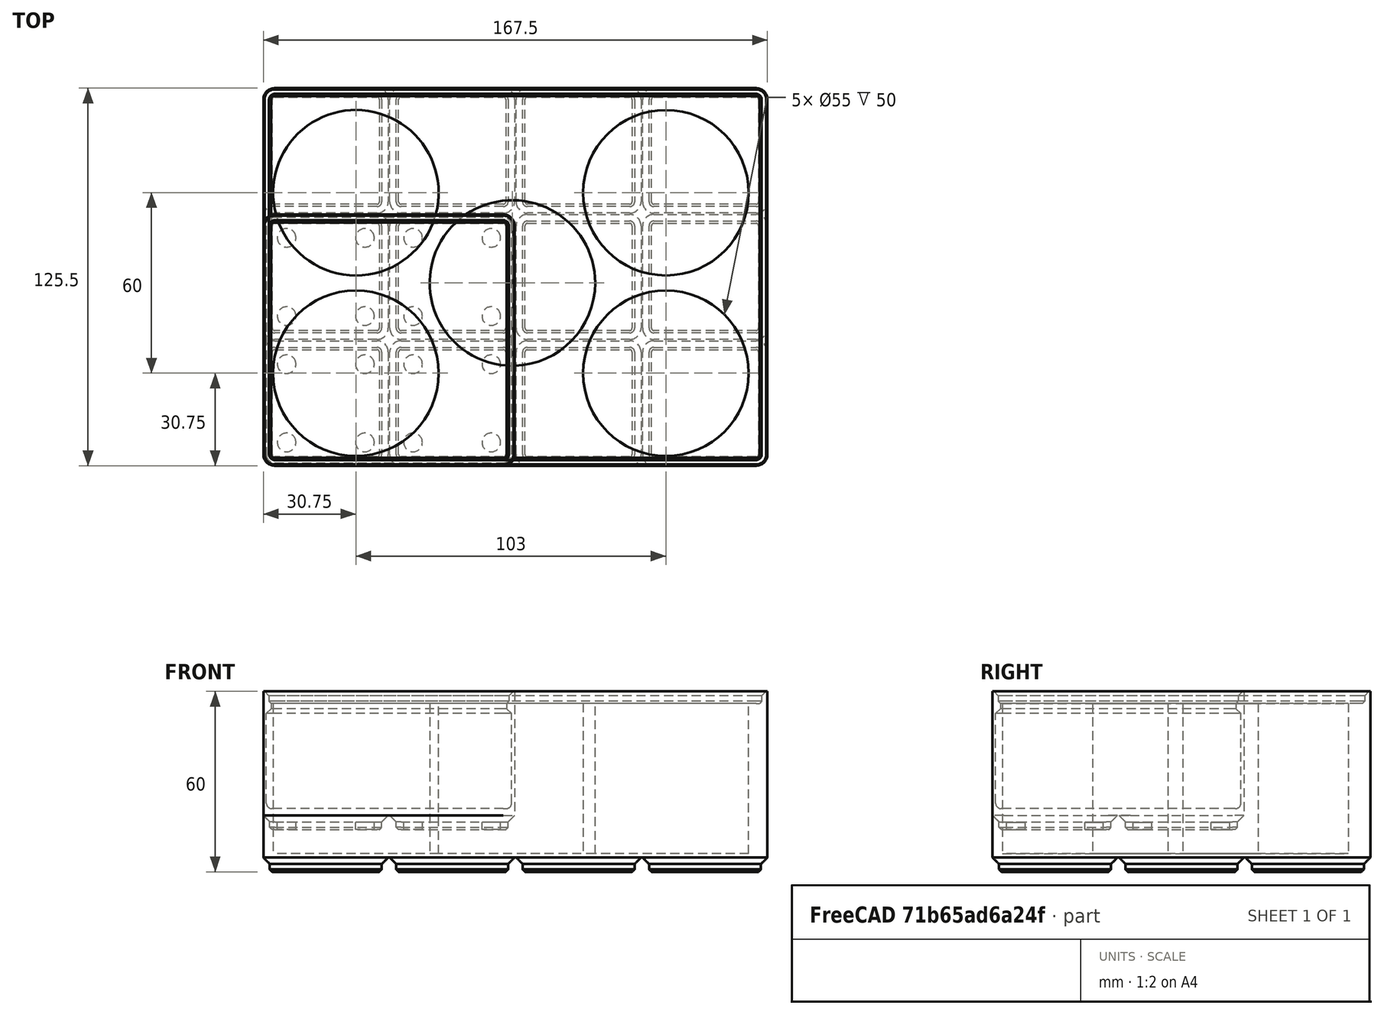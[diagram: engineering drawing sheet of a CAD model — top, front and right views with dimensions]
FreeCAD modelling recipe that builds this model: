
FCSTD DOCUMENT  (FreeCAD 1.0R1.0.1)
Label: Box_3x4x8_5EddingSprays
License: All rights reserved
LicenseURL: http://en.wikipedia.org/wiki/All_rights_reserved
objects: Part::Cylinder×5, Part::FeaturePython×2, Part::MultiFuse×1, Part::Cut×1
note: 9 computed .brp shape members not serialized (recipe doc carries the construction recipe); baked Part::Feature solids carry a one-line shape summary decoded from their .brp

FEATURE [Part::FeaturePython] SimpleStorageBin  # WARN: FeaturePython — macro-defined, semantics opaque (R4)
  BaseProfileBottomChamfer = 0.8
  BaseProfileHeight = 4.75
  BaseProfileTopChamfer = 2.15
  BaseProfileVerticalSection = 1.8
  Baseplate = false
  BinBottomRadius = 0.8
  BinOuterRadius = 3.75
  BinVerticalRadius = 1.6
  Clearance = 0.25
  CustomHeight = 42
  DividerThickness = 1.2
  GenerationLocation = 0
  HeightUnitValue = 7
  HeightUnits = 6
  InsideFilletRadius = 1.85
  LabelShelfAngle = 45
  LabelShelfLength = 42
  LabelShelfPlacement = 0
  LabelShelfStackingOffset = 0.4
  LabelShelfStyle = 0
  LabelShelfVerticalThickness = 1.2
  LabelShelfWidth = 12
  MagnetHoleDepth = 2.4
  MagnetHoleDiameter = 6.2
  MagnetHoleDistanceFromEdge = 8
  MagnetHoles = true
  MagnetHolesShape = 0
  NonStandardHeight = false
  Scoop = false
  ScoopRadius = 21
  ScrewHoleDepth = 6
  ScrewHoleDiameter = 3
  ScrewHoles = false
  SequentialBridgingLayerHeight = 0.2
  StackingLip = true
  StackingLipBottomChamfer = 0.7
  StackingLipTopChamfer = 1.5
  StackingLipTopLedge = 0.4
  StackingLipVerticalSection = 1.8
  TotalHeight = 42
  UsableHeight = 35
  WallThickness = 1
  version = 0.11.9
  xDividerHeight = 0
  xDividers = 0
  xGridSize = 42
  xGridUnits = 2
  xLocationOffset = 0
  xTotalWidth = 83.5
  yDividerHeight = 0
  yDividers = 0
  yGridSize = 42
  yGridUnits = 2
  yLocationOffset = 0
  yTotalWidth = 83.5
  expr: BaseProfileHeight = BaseProfileBottomChamfer + BaseProfileVerticalSection + BaseProfileTopChamfer
  expr: TotalHeight = NonStandardHeight == 1 ? CustomHeight : HeightUnits * HeightUnitValue
  expr: xTotalWidth = xGridUnits * xGridSize - (Baseplate == 1 ? 0 mm : 2 * Clearance)
  expr: yTotalWidth = yGridUnits * yGridSize - (Baseplate == 1 ? 0 mm : 2 * Clearance)
FEATURE [Part::FeaturePython] BinBlank  # WARN: FeaturePython — macro-defined, semantics opaque (R4)
  BaseProfileBottomChamfer = 0.8
  BaseProfileHeight = 4.75
  BaseProfileTopChamfer = 2.15
  BaseProfileVerticalSection = 1.8
  Baseplate = false
  BinBottomRadius = 0.8
  BinOuterRadius = 3.75
  BinVerticalRadius = 1.6
  Clearance = 0.25
  CustomHeight = 42
  GenerationLocation = 0
  HeightUnitValue = 7
  HeightUnits = 8
  MagnetHoleDepth = 2.4
  MagnetHoleDiameter = 6.2
  MagnetHoleDistanceFromEdge = 8
  MagnetHoles = false
  MagnetHolesShape = 0
  NonStandardHeight = false
  RecessedTopDepth = 0
  ScrewHoleDepth = 6
  ScrewHoleDiameter = 3
  ScrewHoles = false
  SequentialBridgingLayerHeight = 0.2
  StackingLip = true
  StackingLipBottomChamfer = 0.7
  StackingLipTopChamfer = 1.5
  StackingLipTopLedge = 0.4
  StackingLipVerticalSection = 1.8
  TotalHeight = 56
  WallThickness = 1
  version = 0.11.9
  xGridSize = 42
  xGridUnits = 4
  xLocationOffset = 0
  xTotalWidth = 167.5
  yGridSize = 42
  yGridUnits = 3
  yLocationOffset = 0
  yTotalWidth = 125.5
  expr: BaseProfileHeight = BaseProfileBottomChamfer + BaseProfileVerticalSection + BaseProfileTopChamfer
  expr: TotalHeight = NonStandardHeight == 1 ? CustomHeight : HeightUnits * HeightUnitValue
  expr: xTotalWidth = xGridUnits * xGridSize - (Baseplate == 1 ? 0 mm : 2 * Clearance)
  expr: yTotalWidth = yGridUnits * yGridSize - (Baseplate == 1 ? 0 mm : 2 * Clearance)
FEATURE [Part::Cylinder] Cylinder
  Angle = 360
  AttacherType = Attacher::AttachEngine3D
  FirstAngle = 0
  Height = 56
  Placement = pos=(31,91,-50) rot=(0,0,1;0rad)
  Radius = 27.5
  SecondAngle = 0
FEATURE [Part::Cylinder] Cylinder001
  Angle = 360
  AttacherType = Attacher::AttachEngine3D
  FirstAngle = 0
  Height = 56
  Placement = pos=(31,31,-50) rot=(0,0,1;0rad)
  Radius = 27.5
  SecondAngle = 0
FEATURE [Part::Cylinder] Cylinder002
  Angle = 360
  AttacherType = Attacher::AttachEngine3D
  FirstAngle = 0
  Height = 56
  Placement = pos=(83,61,-50) rot=(0,0,1;0rad)
  Radius = 27.5
  SecondAngle = 0
FEATURE [Part::Cylinder] Cylinder004
  Angle = 360
  AttacherType = Attacher::AttachEngine3D
  FirstAngle = 0
  Height = 56
  Placement = pos=(134,91,-50) rot=(0,0,1;0rad)
  Radius = 27.5
  SecondAngle = 0
FEATURE [Part::Cylinder] Cylinder005
  Angle = 360
  AttacherType = Attacher::AttachEngine3D
  FirstAngle = 0
  Height = 56
  Placement = pos=(134,31,-50) rot=(0,0,1;0rad)
  Radius = 27.5
  SecondAngle = 0
FEATURE [Part::MultiFuse] Fusion
  Shapes = -> [Cylinder,Cylinder001,Cylinder002,Cylinder004,Cylinder005]
FEATURE [Part::Cut] Cut
  Base = -> BinBlank
  Tool = -> Fusion
